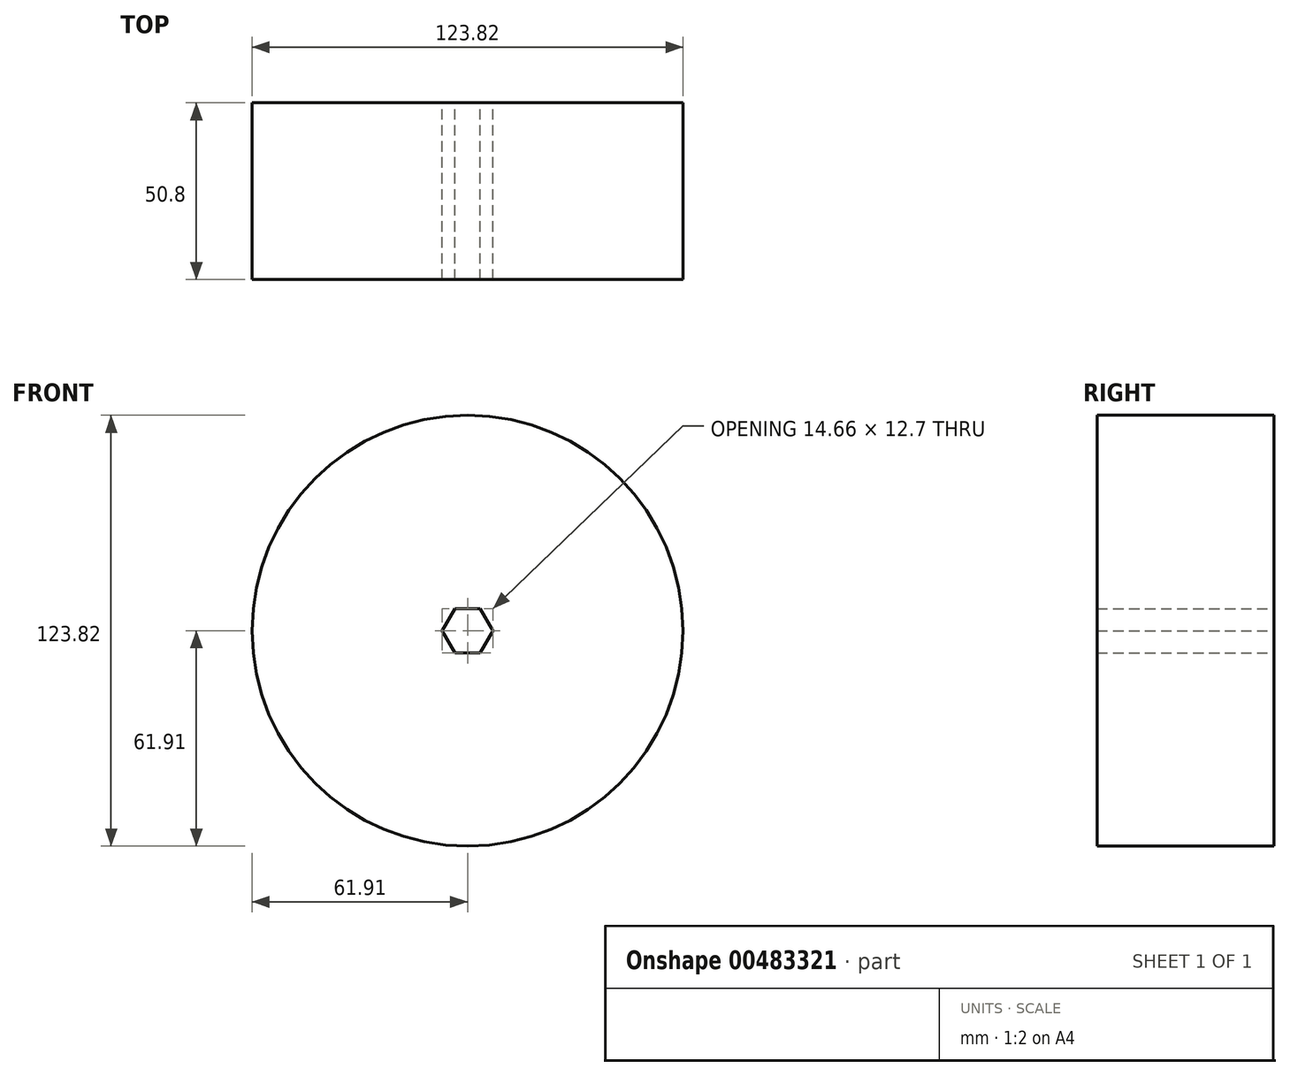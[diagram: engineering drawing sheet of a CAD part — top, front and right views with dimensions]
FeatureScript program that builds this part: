
annotation { "Feature Type Name" : "Feature", "Feature Type Description" : "" }
export const myFeature = defineFeature(function(context is Context, id is Id, definition is map)
    precondition{}
    {
        {
            var Q0;
            Q0=qCreatedBy(makeId("Front.planeOp"),FACE);
            var sketch = newSketch(context, id + "F0", { "sketchPlane" : qUnion([Q0])});
            skCircle(sketch, "E0", {"center": v(0, 0) * mm, "radius": 61.91 * mm});
            skCircle(sketch, "E1.cCircle", {"center": v(0, 0) * mm, "radius": 6.35 * mm, "construction": true});
            skLineSegment(sketch, "E1.0", {"start": v(-3.67, 6.35) * mm, "end": v(3.67, 6.35) * mm});
            skLineSegment(sketch, "E1.1", {"start": v(3.67, 6.35) * mm, "end": v(7.33, 0) * mm});
            skLineSegment(sketch, "E1.2", {"start": v(7.33, 0) * mm, "end": v(3.67, -6.35) * mm});
            skLineSegment(sketch, "E1.3", {"start": v(3.67, -6.35) * mm, "end": v(-3.67, -6.35) * mm});
            skLineSegment(sketch, "E1.4", {"start": v(-3.67, -6.35) * mm, "end": v(-7.33, 0) * mm});
            skLineSegment(sketch, "E1.5", {"start": v(-7.33, 0) * mm, "end": v(-3.67, 6.35) * mm});
            skPoint(sketch, "E1.0.midPoint", {"position": v(0, 6.35) * mm});
            skSolve(sketch);
        }
        {
            var Q0;
            Q0 = qSketchRegion(id + "F0", true);
            extrude(context, id + "F1", {"entities" : qUnion([Q0]), "endBound" : BoundingType.SYMMETRIC, "depth" : 50.8 * mm});
        }
    });
